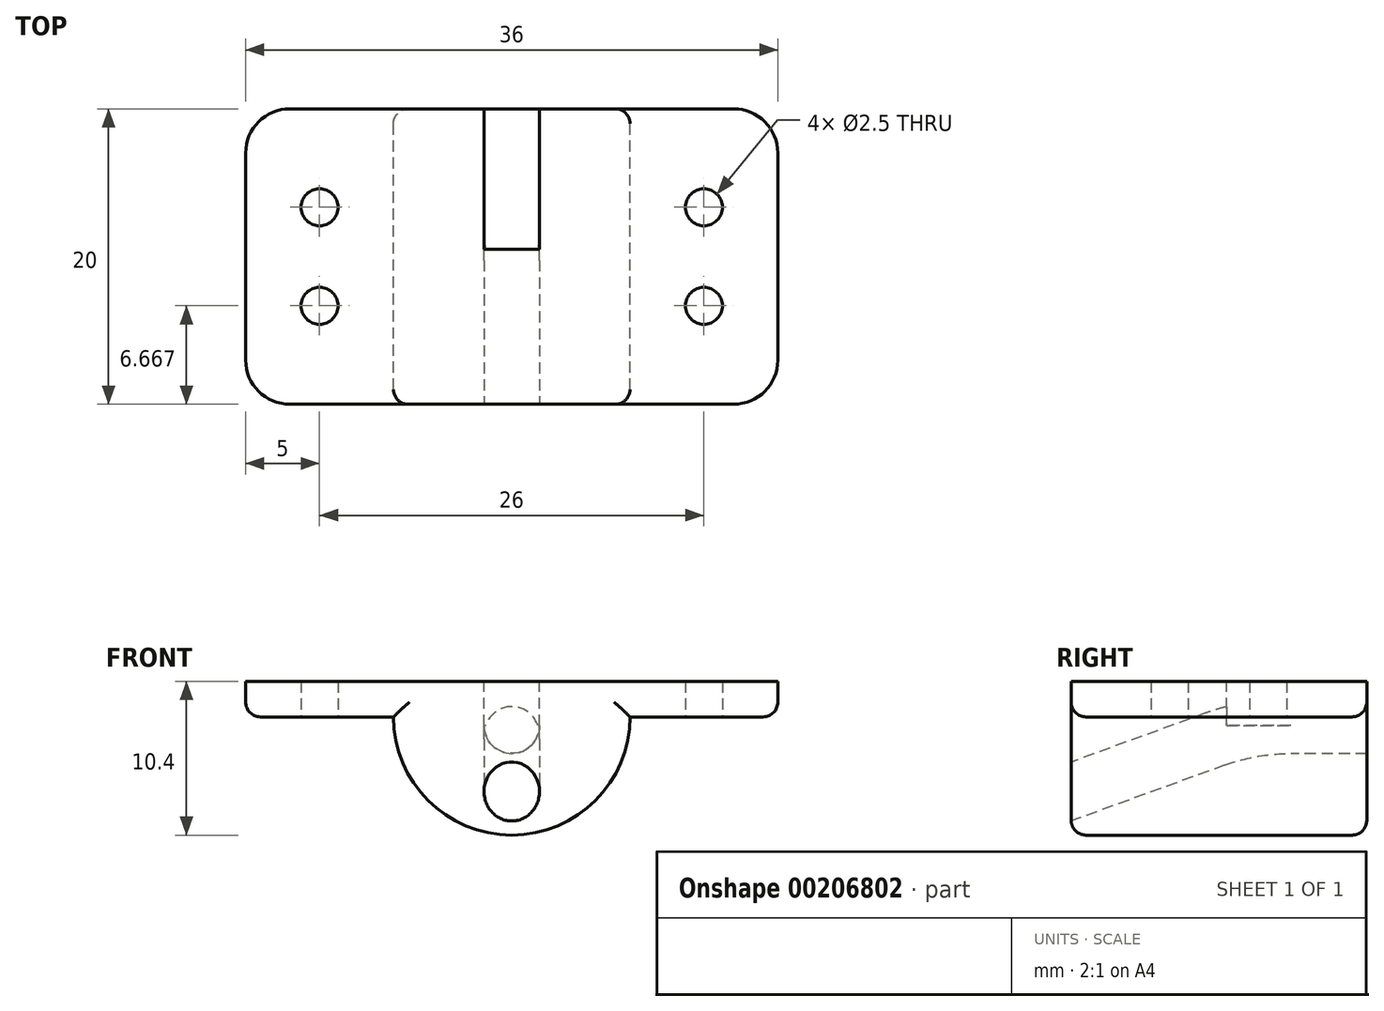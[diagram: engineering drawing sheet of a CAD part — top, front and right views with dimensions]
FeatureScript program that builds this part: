
annotation { "Feature Type Name" : "Feature", "Feature Type Description" : "" }
export const myFeature = defineFeature(function(context is Context, id is Id, definition is map)
    precondition{}
    {
        {
            var Q0;
            Q0=qCreatedBy(makeId("Top.planeOp"),FACE);
            var sketch = newSketch(context, id + "F0", { "sketchPlane" : qUnion([Q0])});
            skLineSegment(sketch, "E0", {"start": v(-38, 0) * mm, "end": v(0, 0) * mm, "construction": true});
            skSolve(sketch);
        }
        {
            var Q0;
            Q0=qCreatedBy(makeId("Front.planeOp"),FACE);
            var sketch = newSketch(context, id + "F1", { "sketchPlane" : qUnion([Q0])});
            skLineSegment(sketch, "E1", {"start": v(0, 0) * mm, "end": v(-18, 0) * mm});
            skLineSegment(sketch, "E2", {"start": v(-18, 0) * mm, "end": v(-18, -2.4) * mm});
            skLineSegment(sketch, "E3", {"start": v(-18, -2.4) * mm, "end": v(-8, -2.4) * mm});
            skArc(sketch, "E4.0", {"start": v(-8, -2.4) * mm, "mid": v(0, -10.4) * mm, "end": v(8, -2.4) * mm});
            skLineSegment(sketch, "E5.MirrorCS", {"start": v(0, 0) * mm, "end": v(18, 0) * mm});
            skLineSegment(sketch, "E6.MirrorCS", {"start": v(18, -2.4) * mm, "end": v(8, -2.4) * mm});
            skLineSegment(sketch, "E7.MirrorCS", {"start": v(18, 0) * mm, "end": v(18, -2.4) * mm});
            skSolve(sketch);
        }
        {
            var Q0;
            Q0=qSketchRegion(id+"F1",true);
            extrude(context, id + "F2", {"entities" : qUnion([Q0]), "depth" : 20 * mm});
        }
        {
            var Q0;
            Q0=qCreatedBy(makeId("Right.planeOp"),FACE);
            var sketch = newSketch(context, id + "F3", { "sketchPlane" : qUnion([Q0])});
            skLineSegment(sketch, "E8", {"start": v(-24.86, -9.22) * mm, "end": v(-10.26, -3.9) * mm});
            skArc(sketch, "E9", {"start": v(-5.13, -3) * mm, "mid": v(-7.74, -3.23) * mm, "end": v(-10.26, -3.9) * mm});
            skLineSegment(sketch, "E10", {"start": v(0, 0) * mm, "end": v(0, -13.95) * mm, "construction": true});
            skLineSegment(sketch, "E11", {"start": v(-5.13, -3) * mm, "end": v(0, -3) * mm});
            skPoint(sketch, "E12.orphan", {"position": v(0, -3.9) * mm});
            skSolve(sketch);
        }
        {
            var Q0;
            Q0=makeQuery(id+"F2.opExtrude","CAP_FACE",FACE,{"disambiguationData":[OSD([sQuery(id+"F1.wireOp",EDGE,"E1"),sQuery(id+"F1.wireOp",EDGE,"E2"),sQuery(id+"F1.wireOp",EDGE,"E3"),sQuery(id+"F1.wireOp",EDGE,"E4.0"),sQuery(id+"F1.wireOp",EDGE,"E5.MirrorCS"),sQuery(id+"F1.wireOp",EDGE,"E6.MirrorCS"),sQuery(id+"F1.wireOp",EDGE,"E7.MirrorCS")])],"isStart":true});
            var sketch = newSketch(context, id + "F4", { "sketchPlane" : qUnion([Q0])});
            skCircle(sketch, "E13", {"center": v(0, -3) * mm, "radius": 1.88 * mm});
            skSolve(sketch);
        }
        {
            var Q0;
            Q0=makeQuery(id+"F4.imprint","IMPRINT",FACE,{"disambiguationData":[TD([[makeQuery(id+"F4.imprint","IMPRINT",EDGE,{"derivedFrom":sQuery(id+"F4.wireOp",EDGE,"E13")}),1.0]])]});
            var Q1;
            Q1=sQuery(id+"F4.wireOp",EDGE,"E13");
            var Q2;
            Q2=sQuery(id+"F3.wireOp",EDGE,"E11");
            var Q3;
            Q3=sQuery(id+"F3.wireOp",EDGE,"E9");
            var Q4;
            Q4=sQuery(id+"F3.wireOp",EDGE,"E8");
            var Q5;
            Q5=sQuery(id+"F3.wireOp",EDGE,"E11");
            var Q6;
            Q6=sQuery(id+"F3.wireOp",EDGE,"E9");
            var Q7;
            Q7=sQuery(id+"F3.wireOp",EDGE,"E8");
            sweep(context, id + "F5", {"operationType" : NewBodyOperationType.REMOVE, "profiles" : qUnion([Q0]), "surfaceProfiles" : qUnion([Q1, Q2, Q3, Q4]), "path" : qUnion([Q5, Q6, Q7])});
        }
        {
            var Q0;
            Q0=makeQuery(id+"F2.opExtrude","SWEPT_FACE",FACE,{"disambiguationData":[OSD([sQuery(id+"F1.wireOp",EDGE,"E1"),sQuery(id+"F1.wireOp",EDGE,"E5.MirrorCS")])]});
            var sketch = newSketch(context, id + "F6", { "sketchPlane" : qUnion([Q0])});
            skLineSegment(sketch, "E14.0", {"start": v(0, -5.13) * mm, "end": v(0, 0) * mm, "construction": true});
            skLineSegment(sketch, "E15.0", {"start": v(0, -5.13) * mm, "end": v(0, -10.26) * mm, "construction": true});
            skLineSegment(sketch, "E16.0", {"start": v(0, -24.86) * mm, "end": v(0, -10.26) * mm, "construction": true});
            skLineSegment(sketch, "E17.0", {"start": v(1.88, -5.13) * mm, "end": v(1.88, 0) * mm});
            skLineSegment(sketch, "E18.0", {"start": v(1.88, -5.13) * mm, "end": v(1.88, -9.5) * mm});
            skLineSegment(sketch, "E19.MirrorCS", {"start": v(-1.88, -5.13) * mm, "end": v(-1.88, 0) * mm});
            skLineSegment(sketch, "E20.MirrorCS", {"start": v(-1.88, -5.13) * mm, "end": v(-1.87, -9.5) * mm});
            skLineSegment(sketch, "E21", {"start": v(1.88, 0) * mm, "end": v(-1.88, 0) * mm});
            skLineSegment(sketch, "E22", {"start": v(1.88, -9.5) * mm, "end": v(-1.88, -9.5) * mm});
            skLineSegment(sketch, "E23.0", {"start": v(-38, 0) * mm, "end": v(0, 0) * mm, "construction": true});
            skSolve(sketch);
        }
        {
            var Q0;
            Q0=qSketchRegion(id+"F6",true);
            var Q1;
            Q1=makeQuery(id+"F5.boolean.opBoolean","COPY",FACE,{"derivedFrom":makeQuery(id+"F5.opSweep","SWEPT_FACE",FACE,{"disambiguationData":[OSD([sQuery(id+"F3.wireOp",EDGE,"E9"),sQuery(id+"F4.wireOp",EDGE,"E13")])]})});
            extrude(context, id + "F7", {"entities" : qUnion([Q0]), "operationType" : NewBodyOperationType.REMOVE, "oppositeDirection" : true, "endBoundEntityFace" : qUnion([Q1]), "depth" : 3 * mm});
        }
        {
            var Q0;
            Q0=makeQuery(id+"F2.opExtrude","SWEPT_FACE",FACE,{"disambiguationData":[OSD([sQuery(id+"F1.wireOp",EDGE,"E6.MirrorCS")])]});
            var sketch = newSketch(context, id + "F8", { "sketchPlane" : qUnion([Q0])});
            skLineSegment(sketch, "E24", {"start": v(13, 20) * mm, "end": v(13, 13.33) * mm, "construction": true});
            skLineSegment(sketch, "E25", {"start": v(13, 13.33) * mm, "end": v(13, 6.67) * mm, "construction": true});
            skLineSegment(sketch, "E26", {"start": v(13, 6.67) * mm, "end": v(13, 0) * mm, "construction": true});
            skCircle(sketch, "E27", {"center": v(13, 13.33) * mm, "radius": 1.25 * mm});
            skCircle(sketch, "E28", {"center": v(13, 6.67) * mm, "radius": 1.25 * mm});
            skCircle(sketch, "E29.MirrorC", {"center": v(-13, 13.33) * mm, "radius": 1.25 * mm});
            skCircle(sketch, "E30.MirrorC", {"center": v(-13, 6.67) * mm, "radius": 1.25 * mm});
            skSolve(sketch);
        }
        {
            var Q0;
            Q0=qSketchRegion(id+"F8",true);
            extrude(context, id + "F9", {"entities" : qUnion([Q0]), "operationType" : NewBodyOperationType.REMOVE, "endBound" : BoundingType.THROUGH_ALL, "oppositeDirection" : true, "depth" : 25 * mm});
        }
        {
            var Q0;
            Q0=makeQuery(id+"F2.opExtrude","CAP_EDGE",EDGE,{"disambiguationData":[OSD([sQuery(id+"F1.wireOp",EDGE,"E7.MirrorCS")])],"isStart":false});
            var Q1;
            Q1=makeQuery(id+"F2.opExtrude","CAP_EDGE",EDGE,{"disambiguationData":[OSD([sQuery(id+"F1.wireOp",EDGE,"E7.MirrorCS")])],"isStart":true});
            var Q2;
            Q2=makeQuery(id+"F2.opExtrude","CAP_EDGE",EDGE,{"disambiguationData":[OSD([sQuery(id+"F1.wireOp",EDGE,"E2")])],"isStart":false});
            var Q3;
            Q3=makeQuery(id+"F2.opExtrude","CAP_EDGE",EDGE,{"disambiguationData":[OSD([sQuery(id+"F1.wireOp",EDGE,"E2")])],"isStart":true});
            fillet(context, id + "F10", {"entities" : qUnion([Q0, Q1, Q2, Q3]), "radius" : 3 * mm, "tangentPropagation" : true, "allowEdgeOverflow" : false});
        }
        {
            var Q0;
            Q0=makeQuery(id+"F2.opExtrude","CAP_EDGE",EDGE,{"disambiguationData":[OSD([sQuery(id+"F1.wireOp",EDGE,"E4.0")])],"isStart":false});
            var Q1;
            Q1=makeQuery(id+"F2.opExtrude","CAP_EDGE",EDGE,{"disambiguationData":[OSD([sQuery(id+"F1.wireOp",EDGE,"E3")])],"isStart":false});
            var Q2;
            Q2=makeQuery(id+"F2.opExtrude","CAP_EDGE",EDGE,{"disambiguationData":[OSD([sQuery(id+"F1.wireOp",EDGE,"E6.MirrorCS")])],"isStart":false});
            var Q3;
            Q3=makeQuery(id+"F2.opExtrude","CAP_EDGE",EDGE,{"disambiguationData":[OSD([sQuery(id+"F1.wireOp",EDGE,"E4.0")])],"isStart":true});
            fillet(context, id + "F11", {"entities" : qUnion([Q0, Q1, Q2, Q3]), "radius" : 1 * mm, "tangentPropagation" : true, "allowEdgeOverflow" : false});
        }
    });
